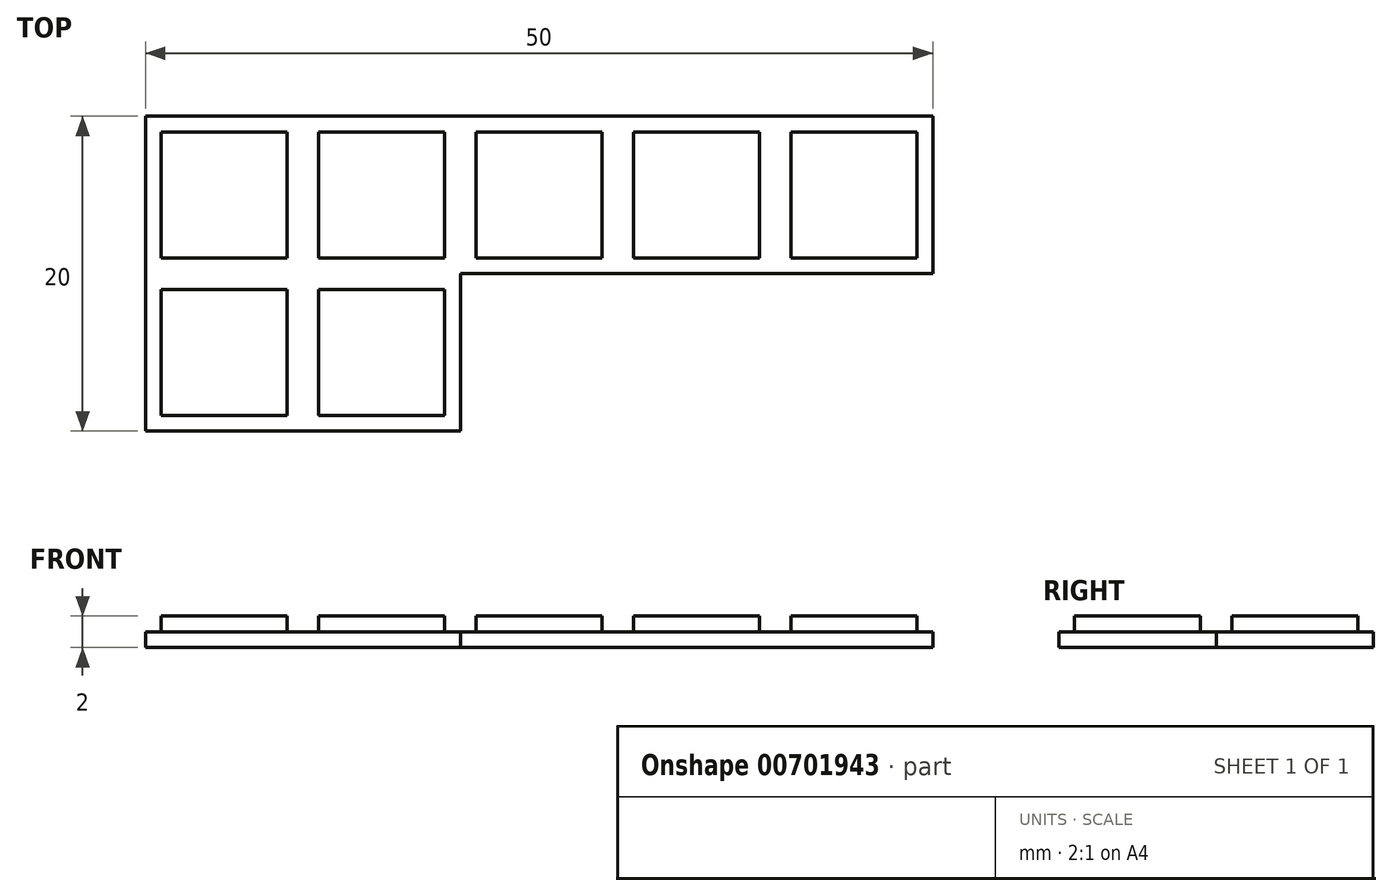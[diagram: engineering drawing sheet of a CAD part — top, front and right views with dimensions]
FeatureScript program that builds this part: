
annotation { "Feature Type Name" : "Feature", "Feature Type Description" : "" }
export const myFeature = defineFeature(function(context is Context, id is Id, definition is map)
    precondition{}
    {
        {
            var Q0;
            Q0=qCreatedBy(makeId("Top.planeOp"),FACE);
            var sketch = newSketch(context, id + "F0", { "sketchPlane" : qUnion([Q0])});
            skLineSegment(sketch, "E0", {"start": v(-20, 10) * mm, "end": v(-20, -10) * mm});
            skLineSegment(sketch, "E1", {"start": v(-20, -10) * mm, "end": v(0, -10) * mm});
            skLineSegment(sketch, "E2", {"start": v(0, -10) * mm, "end": v(0, 0) * mm});
            skLineSegment(sketch, "E3", {"start": v(0, 0) * mm, "end": v(30, 0) * mm});
            skLineSegment(sketch, "E4", {"start": v(30, 0) * mm, "end": v(30, 10) * mm});
            skLineSegment(sketch, "E5", {"start": v(30, 10) * mm, "end": v(-20, 10) * mm});
            skSolve(sketch);
        }
        {
            var Q0;
            Q0=makeQuery(id+"F0.imprint","IMPRINT",FACE,{"disambiguationData":[TD([[makeQuery(id+"F0.imprint","IMPRINT",EDGE,{"derivedFrom":sQuery(id+"F0.wireOp",EDGE,"qFyTJhzL-X8oy-V4Zn-n2UO-jb0vi0Htoton")}),1.0]])]});
            var Q1;
            Q1=makeQuery(id+"F0.imprint","IMPRINT",FACE,{"disambiguationData":[TD([[makeQuery(id+"F0.imprint","IMPRINT",EDGE,{"derivedFrom":sQuery(id+"F0.wireOp",EDGE,"E0")}),1.0]])]});
            var Q2;
            Q2=makeQuery(id+"F0.imprint","IMPRINT",FACE,{"disambiguationData":[TD([[makeQuery(id+"F0.imprint","IMPRINT",EDGE,{"derivedFrom":sQuery(id+"F0.wireOp",EDGE,"WSVu92h9-HOxL-UAjn-v7h9-4ASb6rVnE2tI")}),1.0]])]});
            var Q3;
            Q3=makeQuery(id+"F0.imprint","IMPRINT",FACE,{"disambiguationData":[TD([[makeQuery(id+"F0.imprint","IMPRINT",EDGE,{"derivedFrom":sQuery(id+"F0.wireOp",EDGE,"Ld2wisXk-MDIs-XWBZ-cWGf-ZvUSmQWxL9CZ")}),1.0]])]});
            extrude(context, id + "F1", {"entities" : qUnion([Q0, Q1, Q2, Q3]), "depth" : 1 * mm, "offsetDistance" : 25 * mm});
        }
        {
            var Q0;
            Q0=makeQuery(id+"F1.opExtrude","CAP_FACE",FACE,{"disambiguationData":[OSD([sQuery(id+"F0.wireOp",EDGE,"E0"),sQuery(id+"F0.wireOp",EDGE,"E1"),sQuery(id+"F0.wireOp",EDGE,"E2"),sQuery(id+"F0.wireOp",EDGE,"E3"),sQuery(id+"F0.wireOp",EDGE,"E4"),sQuery(id+"F0.wireOp",EDGE,"E5")])],"isStart":false});
            var sketch = newSketch(context, id + "F2", { "sketchPlane" : qUnion([Q0])});
            skLineSegment(sketch, "E6", {"start": v(-10, 10) * mm, "end": v(-10, -10) * mm, "construction": true});
            skLineSegment(sketch, "E7", {"start": v(0, 0) * mm, "end": v(0, 10) * mm, "construction": true});
            skLineSegment(sketch, "E8", {"start": v(10, 10) * mm, "end": v(10, 0) * mm, "construction": true});
            skLineSegment(sketch, "E9", {"start": v(20, 10) * mm, "end": v(20, 0) * mm, "construction": true});
            skLineSegment(sketch, "E10", {"start": v(0, 0) * mm, "end": v(-20, 0) * mm, "construction": true});
            skLineSegment(sketch, "E11", {"start": v(30, 1) * mm, "end": v(-20, 1) * mm});
            skLineSegment(sketch, "E12", {"start": v(-1, -10) * mm, "end": v(-1, 10) * mm});
            skLineSegment(sketch, "E13", {"start": v(-20, -9) * mm, "end": v(0, -9) * mm});
            skLineSegment(sketch, "E14", {"start": v(-19, -10) * mm, "end": v(-19, 10) * mm});
            skLineSegment(sketch, "E15", {"start": v(-20, 9) * mm, "end": v(30, 9) * mm});
            skLineSegment(sketch, "E16", {"start": v(29, 10) * mm, "end": v(29, 0) * mm});
            skLineSegment(sketch, "E17", {"start": v(1, 0) * mm, "end": v(1, 10) * mm});
            skLineSegment(sketch, "E18", {"start": v(-20, -1) * mm, "end": v(0, -1) * mm});
            skLineSegment(sketch, "E19", {"start": v(-11, 10) * mm, "end": v(-11, -10) * mm});
            skLineSegment(sketch, "E20", {"start": v(-9, 10) * mm, "end": v(-9, -10) * mm});
            skLineSegment(sketch, "E21", {"start": v(9, 10) * mm, "end": v(9, 0) * mm});
            skLineSegment(sketch, "E22", {"start": v(11, 10) * mm, "end": v(11, 0) * mm});
            skLineSegment(sketch, "E23", {"start": v(19, 10) * mm, "end": v(19, 0) * mm});
            skLineSegment(sketch, "E24", {"start": v(21, 10) * mm, "end": v(21, 0) * mm});
            skSolve(sketch);
        }
        {
            var Q0;
            {var subQ0=sQuery(id+"F2.wireOp",EDGE,"E19");var subQ1=sQuery(id+"F2.wireOp",EDGE,"E11");var subQ2=makeQuery(id+"F2.imprint","INTERSECT",VERTEX,{"derivedFrom":[subQ1,subQ0]});Q0=makeQuery(id+"F2.imprint","IMPRINT",FACE,{"disambiguationData":[TD([[makeQuery(id+"F2.imprint","IMPRINT",EDGE,{"disambiguationData":[TD([[subQ2,-1.0]])],"derivedFrom":subQ1}),-1.0]])]});}
            var Q1;
            {var subQ0=sQuery(id+"F2.wireOp",EDGE,"E14");var subQ1=sQuery(id+"F2.wireOp",EDGE,"E13");var subQ2=makeQuery(id+"F2.imprint","INTERSECT",VERTEX,{"derivedFrom":[subQ1,subQ0]});Q1=makeQuery(id+"F2.imprint","IMPRINT",FACE,{"disambiguationData":[TD([[makeQuery(id+"F2.imprint","IMPRINT",EDGE,{"disambiguationData":[TD([[subQ2,-1.0]])],"derivedFrom":subQ1}),1.0]])]});}
            var Q2;
            {var subQ0=sQuery(id+"F2.wireOp",EDGE,"E13");var subQ1=sQuery(id+"F2.wireOp",EDGE,"E12");var subQ2=makeQuery(id+"F2.imprint","INTERSECT",VERTEX,{"derivedFrom":[subQ1,subQ0]});Q2=makeQuery(id+"F2.imprint","IMPRINT",FACE,{"disambiguationData":[TD([[makeQuery(id+"F2.imprint","IMPRINT",EDGE,{"disambiguationData":[TD([[subQ2,-1.0]])],"derivedFrom":subQ1}),1.0]])]});}
            var Q3;
            {var subQ0=sQuery(id+"F2.wireOp",EDGE,"E12");var subQ1=sQuery(id+"F2.wireOp",EDGE,"E11");var subQ2=makeQuery(id+"F2.imprint","INTERSECT",VERTEX,{"derivedFrom":[subQ1,subQ0]});Q3=makeQuery(id+"F2.imprint","IMPRINT",FACE,{"disambiguationData":[TD([[makeQuery(id+"F2.imprint","IMPRINT",EDGE,{"disambiguationData":[TD([[subQ2,-1.0]])],"derivedFrom":subQ1}),-1.0]])]});}
            var Q4;
            {var subQ0=sQuery(id+"F2.wireOp",EDGE,"E21");var subQ1=sQuery(id+"F2.wireOp",EDGE,"E11");var subQ2=makeQuery(id+"F2.imprint","INTERSECT",VERTEX,{"derivedFrom":[subQ1,subQ0]});Q4=makeQuery(id+"F2.imprint","IMPRINT",FACE,{"disambiguationData":[TD([[makeQuery(id+"F2.imprint","IMPRINT",EDGE,{"disambiguationData":[TD([[subQ2,-1.0]])],"derivedFrom":subQ1}),-1.0]])]});}
            var Q5;
            {var subQ0=sQuery(id+"F2.wireOp",EDGE,"E23");var subQ1=sQuery(id+"F2.wireOp",EDGE,"E11");var subQ2=makeQuery(id+"F2.imprint","INTERSECT",VERTEX,{"derivedFrom":[subQ1,subQ0]});Q5=makeQuery(id+"F2.imprint","IMPRINT",FACE,{"disambiguationData":[TD([[makeQuery(id+"F2.imprint","IMPRINT",EDGE,{"disambiguationData":[TD([[subQ2,-1.0]])],"derivedFrom":subQ1}),-1.0]])]});}
            var Q6;
            {var subQ0=sQuery(id+"F2.wireOp",EDGE,"E16");var subQ1=sQuery(id+"F2.wireOp",EDGE,"E11");var subQ2=makeQuery(id+"F2.imprint","INTERSECT",VERTEX,{"derivedFrom":[subQ1,subQ0]});Q6=makeQuery(id+"F2.imprint","IMPRINT",FACE,{"disambiguationData":[TD([[makeQuery(id+"F2.imprint","IMPRINT",EDGE,{"disambiguationData":[TD([[subQ2,-1.0]])],"derivedFrom":subQ1}),-1.0]])]});}
            extrude(context, id + "F3", {"entities" : qUnion([Q0, Q1, Q2, Q3, Q4, Q5, Q6]), "operationType" : NewBodyOperationType.ADD, "depth" : 1 * mm, "offsetDistance" : 25 * mm});
        }
    });
